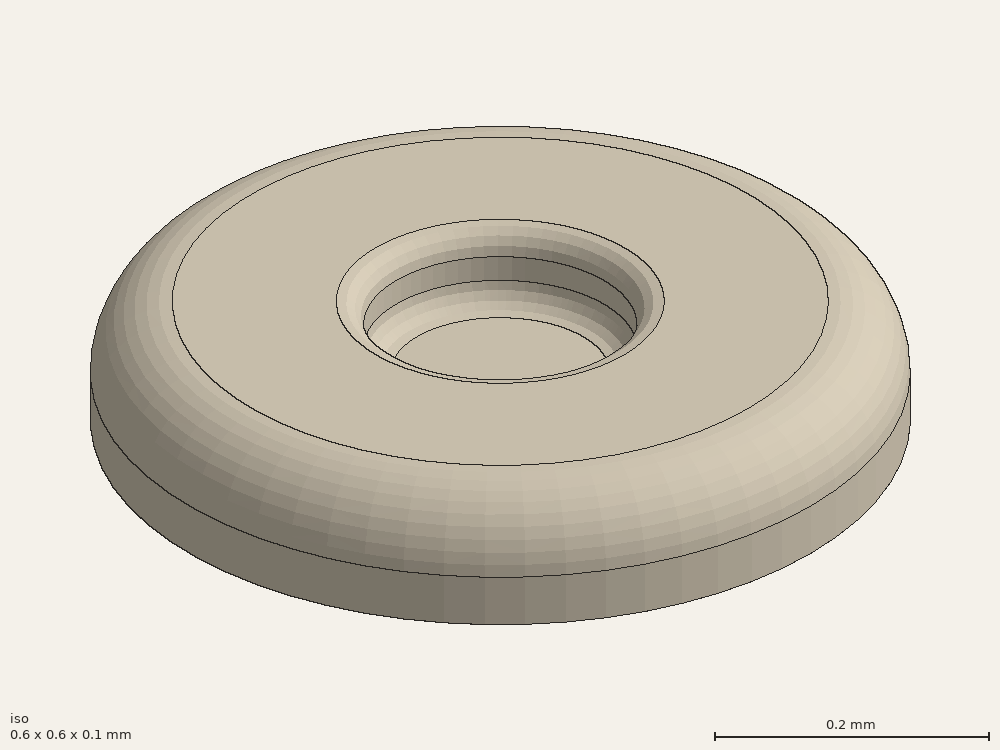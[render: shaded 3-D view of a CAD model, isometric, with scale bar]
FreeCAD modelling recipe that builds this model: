
FCSTD DOCUMENT  (FreeCAD 0.16R6712 (Git))
Label: fixtag
License: All rights reserved
LicenseURL: http://en.wikipedia.org/wiki/All_rights_reserved
objects: Sketcher::SketchObject×2, PartDesign::Fillet×2, PartDesign::Pad×1, PartDesign::Pocket×1, Mesh::Feature×1
note: 8 computed .brp shape members not serialized (recipe doc carries the construction recipe); baked Part::Feature solids carry a one-line shape summary decoded from their .brp

FEATURE [Sketcher::SketchObject] Sketch
  sketch-geometry (1):
    g0: Circle CenterX=0 CenterY=0 CenterZ=0 NormalX=0 NormalY=0 NormalZ=1 Radius=0.3
  constraints (2):
    c: Radius(g0) = 0.3
    c: Coincident(g0,g-1)
FEATURE [PartDesign::Pad] Pad
  Length = 0.1
  Length2 = 100
  Sketch = -> Sketch
  Type = 0
FEATURE [PartDesign::Fillet] Fillet
  Base = -> Pad [Edge3]
  Radius = 0.06
FEATURE [Sketcher::SketchObject] Sketch001
  Placement = pos=(0,0,0.1) rot=(0,0,1;0rad)
  Support = -> Fillet [Face4]
  sketch-geometry (1):
    g0: Circle CenterX=0 CenterY=0 CenterZ=0 NormalX=0 NormalY=0 NormalZ=1 Radius=0.1
  constraints (2):
    c: Coincident(g0,g-1)
    c: Radius(g0) = 0.1
FEATURE [PartDesign::Pocket] Pocket
  Length = 0.06
  Sketch = -> Sketch001
  Type = 0
FEATURE [PartDesign::Fillet] Fillet001
  Base = -> Pocket [Edge6,Edge8]
  Radius = 0.02
FEATURE [Mesh::Feature] Mesh  label="Fillet001 (Meshed)"
